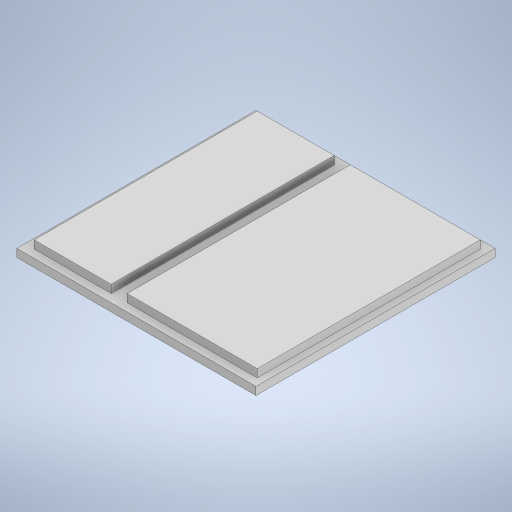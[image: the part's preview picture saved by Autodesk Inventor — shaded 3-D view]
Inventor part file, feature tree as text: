
AUTODESK INVENTOR PART (.ipt)
format: ipt  version: 2024 (Build 280153000, 153)  size: 238,080 bytes
history: native  units: mm
features: extrude x4, sketch x4, other x1
ambient origin geometry x8: Origin, YZ Plane, XZ Plane, XY Plane, X Axis, Y Axis, Z Axis, Center Point
bodies: Body1 (feature_tree)
feature tree (9):
  other  "Těleso1"
  extrude  "Vysunutí1"  Depth=90.0mm
  extrude  "Vysunutí2"  Depth=90.0mm
  extrude  "Vysunutí3"  Depth=3.0mm TaperAngle=0.0deg
  extrude  "Vysunutí4"  Depth=3.5mm
  sketch  "Náčrt1"
  sketch  "Náčrt2"
  sketch  "Náčrt3"
  sketch  "Náčrt6"
